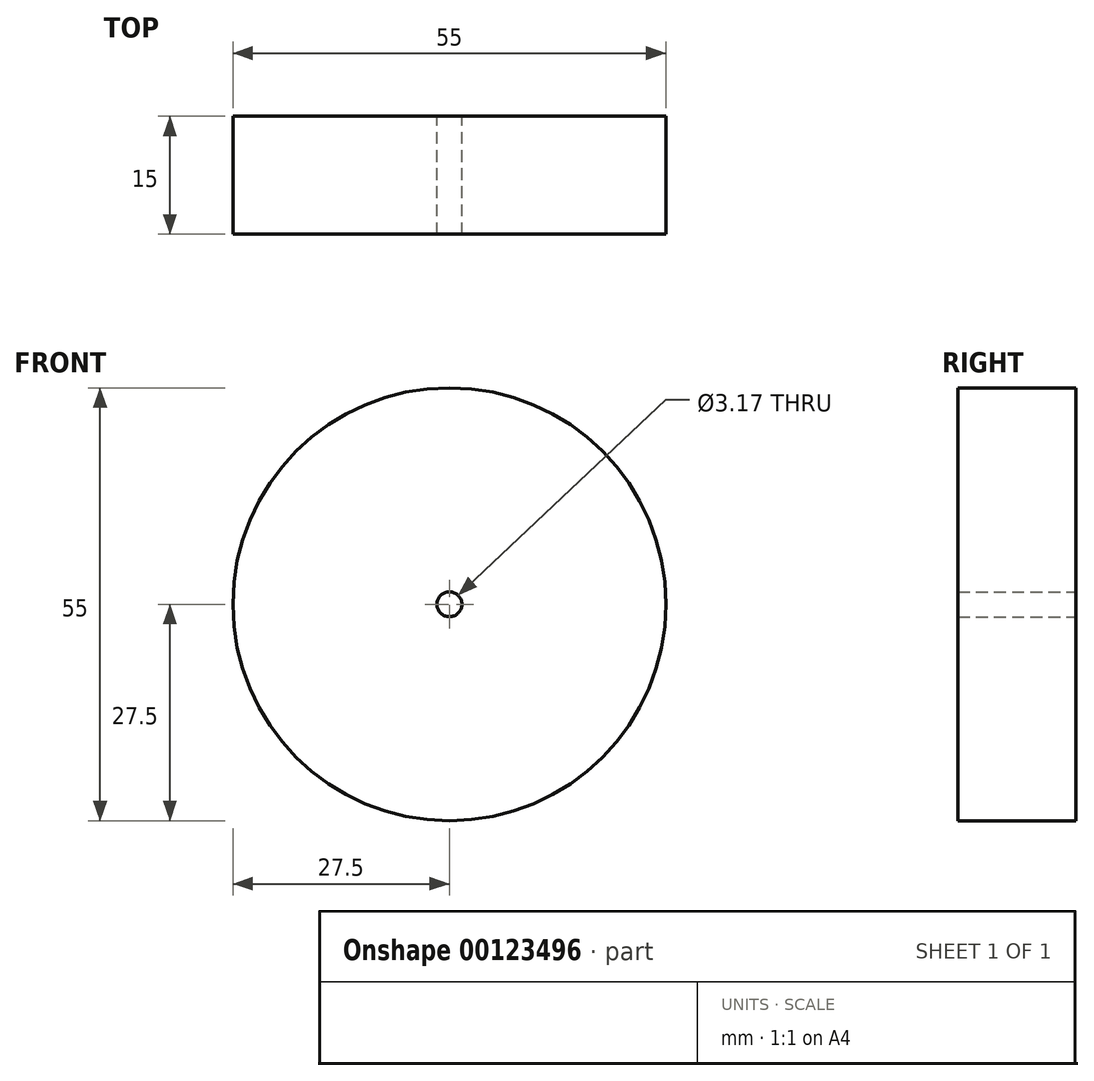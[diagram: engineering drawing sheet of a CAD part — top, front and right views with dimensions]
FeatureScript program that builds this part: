
annotation { "Feature Type Name" : "Feature", "Feature Type Description" : "" }
export const myFeature = defineFeature(function(context is Context, id is Id, definition is map)
    precondition{}
    {
        {
            var Q0;
            Q0=qCreatedBy(makeId("Front.planeOp"),FACE);
            var sketch = newSketch(context, id + "F0", { "sketchPlane" : qUnion([Q0])});
            skCircle(sketch, "E0", {"center": v(0, 0) * mm, "radius": 27.5 * mm});
            skCircle(sketch, "E1", {"center": v(0, 0) * mm, "radius": 1.59 * mm});
            skSolve(sketch);
        }
        {
            var Q0;
            Q0 = qSketchRegion(id + "F0", true);
            extrude(context, id + "F1", {"entities" : qUnion([Q0]), "depth" : 15 * mm});
        }
    });
